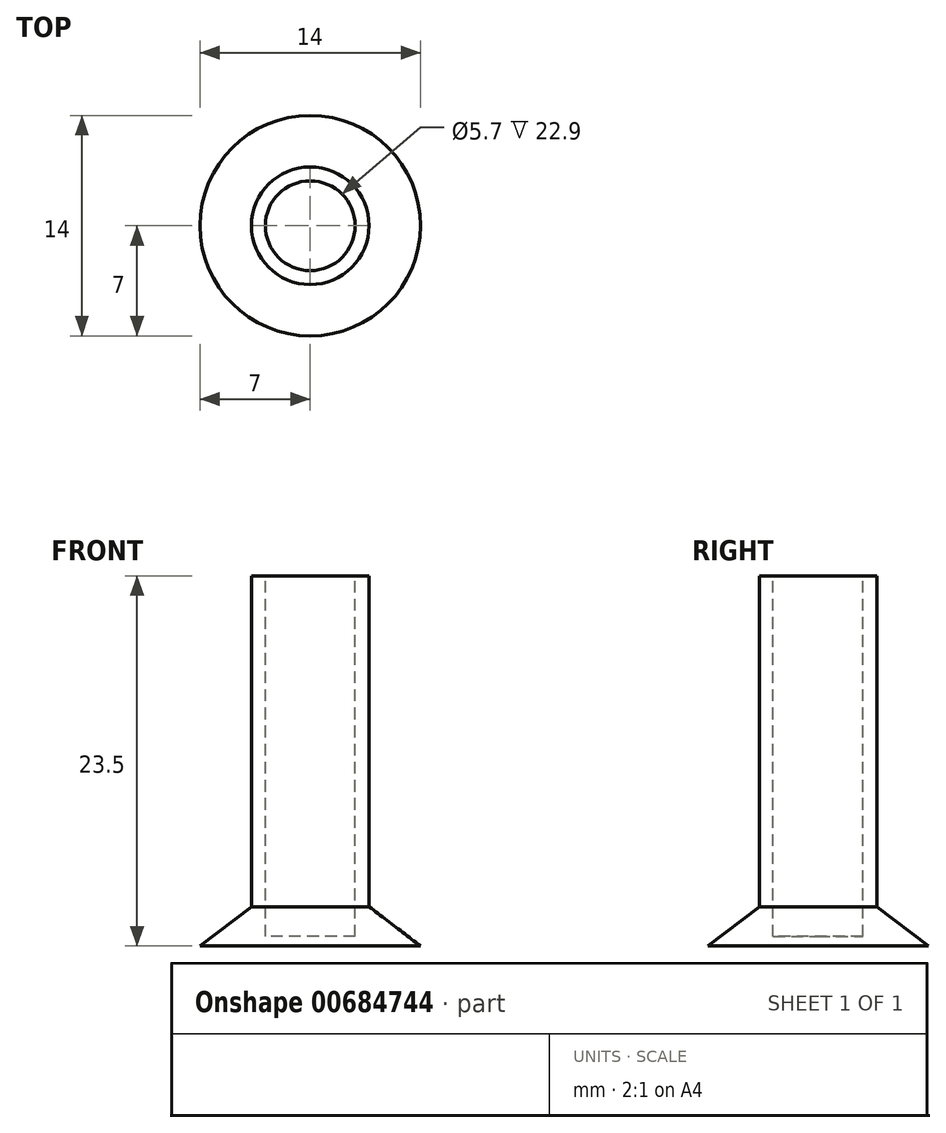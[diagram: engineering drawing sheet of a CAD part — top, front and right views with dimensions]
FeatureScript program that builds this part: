
annotation { "Feature Type Name" : "Feature", "Feature Type Description" : "" }
export const myFeature = defineFeature(function(context is Context, id is Id, definition is map)
    precondition{}
    {
        {
            var Q0;
            Q0=qCreatedBy(makeId("Front.planeOp"),FACE);
            var sketch = newSketch(context, id + "F0", { "sketchPlane" : qUnion([Q0])});
            skLineSegment(sketch, "E0", {"start": v(0, 0.6) * mm, "end": v(0, 0) * mm});
            skLineSegment(sketch, "E1", {"start": v(0, 0) * mm, "end": v(7, 0) * mm});
            skLineSegment(sketch, "E2", {"start": v(2.85, 23.5) * mm, "end": v(3.74, 23.5) * mm});
            skLineSegment(sketch, "E3", {"start": v(2.85, 0.6) * mm, "end": v(0, 0.6) * mm});
            skLineSegment(sketch, "E4", {"start": v(3.74, 23.5) * mm, "end": v(3.74, 2.5) * mm});
            skLineSegment(sketch, "E5", {"start": v(3.74, 2.5) * mm, "end": v(7, 0) * mm});
            skLineSegment(sketch, "E6", {"start": v(2.85, 0.6) * mm, "end": v(2.85, 23.5) * mm});
            skSolve(sketch);
        }
        {
            var Q0;
            Q0=qSketchRegion(id+"F0",true);
            var Q1;
            Q1=sQuery(id+"F0.wireOp",EDGE,"E0");
            revolve(context, id + "F1", {"entities" : qUnion([Q0]), "axis" : qUnion([Q1]), "revolveType" : RevolveType.FULL});
        }
    });
